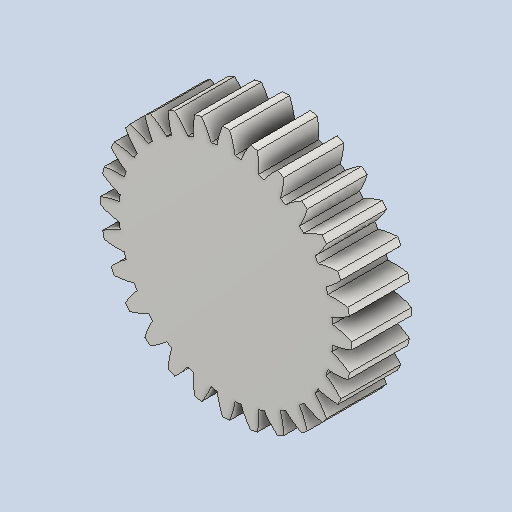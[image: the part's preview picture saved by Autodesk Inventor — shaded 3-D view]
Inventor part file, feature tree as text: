
AUTODESK INVENTOR PART (.ipt)
format: ipt  version: 2024 (Build 280153000, 153)  size: 265,216 bytes
history: native  units: mm (DEFAULTED — no unit token found)
features: plane x3, other x3, extrude x1, sketch x1
ambient origin geometry x8: Origin, YZ Plane, XZ Plane, XY Plane, X Axis, Y Axis, Z Axis, Center Point
bodies: Solid1 (feature_tree)
feature tree (8):
  extrude  "Extrusion1"  Depth=5.0mm TaperAngle=0.0deg
  plane  "Work Plane2"
  plane  "Work Plane8"
  plane  "Work Plane9"
  other  "Spur Gear"
  sketch  "Sketch1"  dims[d0=20.999062mm d1=5.0mm d2=0.0mm d3=19.6mm d4=10.0mm d5=0.0mm d16=20.0mm d17=0.0mm d34=1.121997mm d39=0.0mm d41=0.0mm d43=20.0mm d46=20.0mm d47=0.0mm d48=0.0mm]
  other  "Srf1"
  other  "Pitch Diameter"
